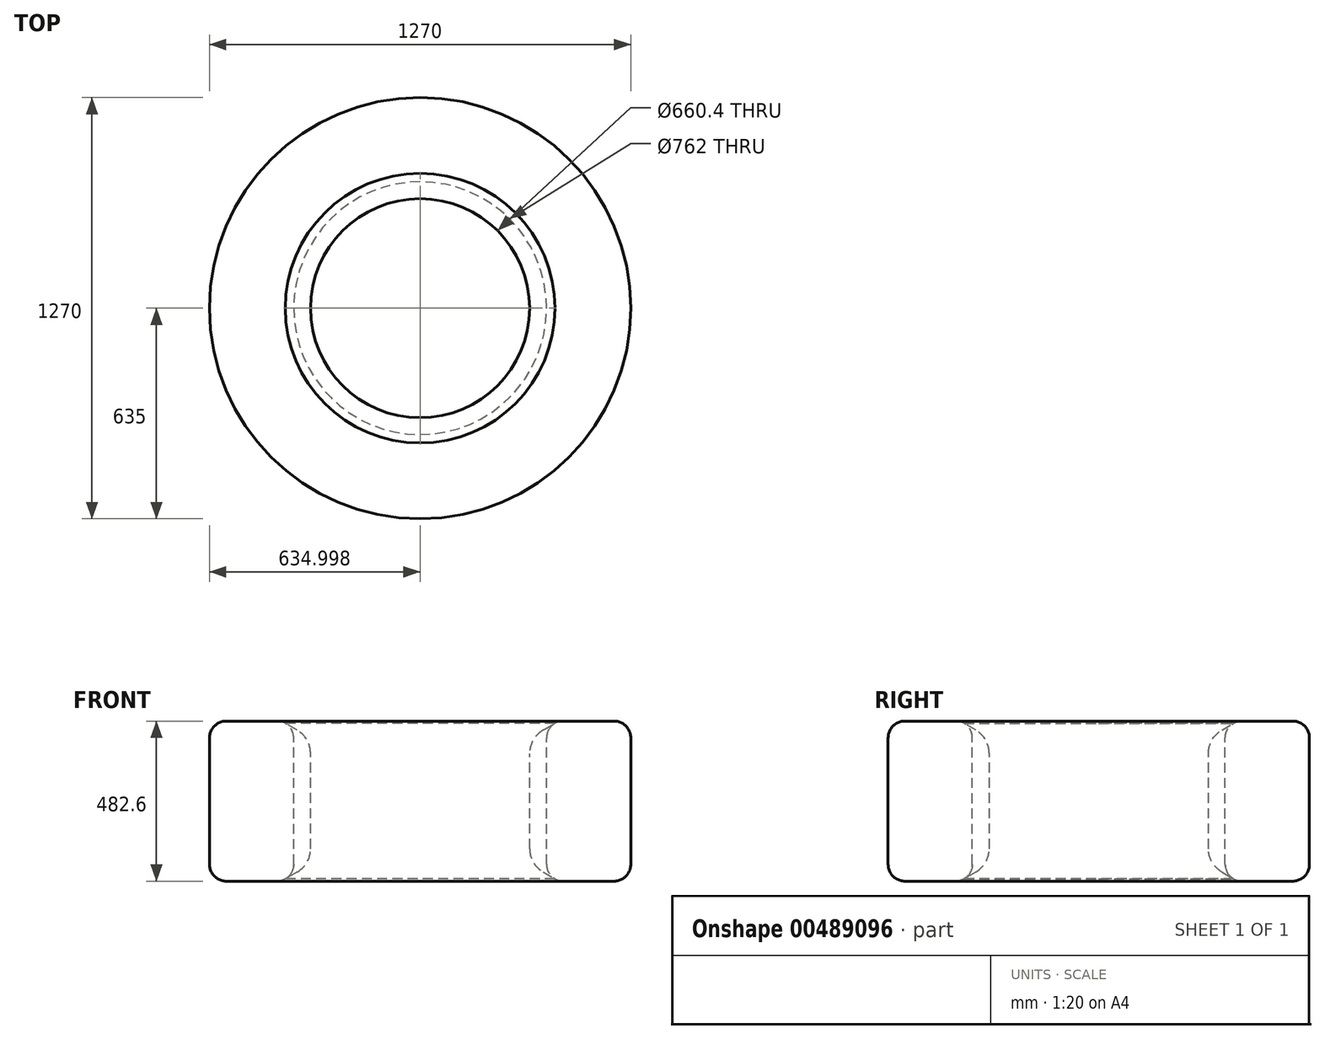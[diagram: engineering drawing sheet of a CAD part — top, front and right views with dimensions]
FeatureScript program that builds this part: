
annotation { "Feature Type Name" : "Feature", "Feature Type Description" : "" }
export const myFeature = defineFeature(function(context is Context, id is Id, definition is map)
    precondition{}
    {
        {
            var Q0;
            Q0=qCreatedBy(makeId("Front.planeOp"),FACE);
            var sketch = newSketch(context, id + "F0", { "sketchPlane" : qUnion([Q0])});
            skLineSegment(sketch, "E0.bottom", {"start": v(-116.08, 399.65) * mm, "end": v(36.32, 399.65) * mm});
            skLineSegment(sketch, "E0.top", {"start": v(-116.08, -82.95) * mm, "end": v(36.32, -82.95) * mm});
            skLineSegment(sketch, "E0.left", {"start": v(-166.88, 348.85) * mm, "end": v(-166.88, -32.15) * mm});
            skLineSegment(sketch, "E0.right", {"start": v(87.12, 348.85) * mm, "end": v(87.12, -32.15) * mm});
            skPoint(sketch, "E1.visualSharp", {"position": v(-166.88, 399.65) * mm});
            skArc(sketch, "E1.filletArc", {"start": v(-116.08, 399.65) * mm, "mid": v(-152, 384.77) * mm, "end": v(-166.88, 348.85) * mm});
            skPoint(sketch, "E2.visualSharp", {"position": v(-166.88, -82.95) * mm});
            skArc(sketch, "E2.filletArc", {"start": v(-166.88, -32.15) * mm, "mid": v(-152, -68.07) * mm, "end": v(-116.08, -82.95) * mm});
            skPoint(sketch, "E3.visualSharp", {"position": v(87.12, 399.65) * mm});
            skArc(sketch, "E3.filletArc", {"start": v(87.12, 348.85) * mm, "mid": v(72.24, 384.77) * mm, "end": v(36.32, 399.65) * mm});
            skPoint(sketch, "E4.visualSharp", {"position": v(87.12, -82.95) * mm});
            skArc(sketch, "E4.filletArc", {"start": v(36.32, -82.95) * mm, "mid": v(72.24, -68.07) * mm, "end": v(87.12, -32.15) * mm});
            skLineSegment(sketch, "E5", {"start": v(-547.88, 440.5) * mm, "end": v(-547.88, -203.24) * mm});
            skSolve(sketch);
        }
        {
            var Q0;
            Q0=makeQuery(id+"F0.imprint","IMPRINT",FACE,{"disambiguationData":[TD([[makeQuery(id+"F0.imprint","IMPRINT",EDGE,{"derivedFrom":sQuery(id+"F0.wireOp",EDGE,"E0.bottom")}),-1.0]])]});
            var Q1;
            Q1=sQuery(id+"F0.wireOp",EDGE,"E5");
            revolve(context, id + "F1", {"entities" : qUnion([Q0]), "axis" : qUnion([Q1]), "revolveType" : RevolveType.FULL});
        }
        {
            var Q0;
            Q0=makeQuery(id+"F0.imprint","IMPRINT",FACE,{"disambiguationData":[TD([[makeQuery(id+"F0.imprint","IMPRINT",EDGE,{"derivedFrom":sQuery(id+"F0.wireOp",EDGE,"E0.bottom")}),-1.0]])]});
            var sketch = newSketch(context, id + "F2", { "sketchPlane" : qUnion([Q0])});
            skLineSegment(sketch, "E6", {"start": v(-217.68, 301.92) * mm, "end": v(-217.68, 14.77) * mm});
            skLineSegment(sketch, "E7", {"start": v(0, 474.53) * mm, "end": v(-177.04, 372.31) * mm});
            skLineSegment(sketch, "E8", {"start": v(-177.04, -55.62) * mm, "end": v(-45.53, -131.55) * mm});
            skPoint(sketch, "E9.orphan", {"position": v(-273.37, 0) * mm});
            skPoint(sketch, "E10.orphan", {"position": v(-217.68, 923.18) * mm});
            skPoint(sketch, "E11.orphan", {"position": v(-217.68, -225.49) * mm});
            skPoint(sketch, "E12.visualSharp", {"position": v(-217.68, 348.85) * mm});
            skArc(sketch, "E12.filletArc", {"start": v(-177.04, 372.31) * mm, "mid": v(-206.8, 342.56) * mm, "end": v(-217.68, 301.92) * mm});
            skPoint(sketch, "E13.visualSharp", {"position": v(-217.68, -32.15) * mm});
            skArc(sketch, "E13.filletArc", {"start": v(-217.68, 14.77) * mm, "mid": v(-206.8, -25.87) * mm, "end": v(-177.04, -55.62) * mm});
            skSolve(sketch);
        }
        {
            var Q0;
            Q0 = qSketchRegion(id + "F2", true);
            var Q1;
            Q1=makeQuery(id+"F2.imprint","IMPRINT",FACE,{"disambiguationData":[TD([[makeQuery(id+"F2.imprint","IMPRINT",EDGE,{"derivedFrom":sQuery(id+"F2.wireOp",EDGE,"E6")}),1.0]])]});
            var Q2;
            Q2=sQuery(id+"F0.wireOp",EDGE,"E5");
            revolve(context, id + "F3", {"entities" : qUnion([Q0, Q1]), "axis" : qUnion([Q2]), "revolveType" : RevolveType.FULL});
        }
    });
